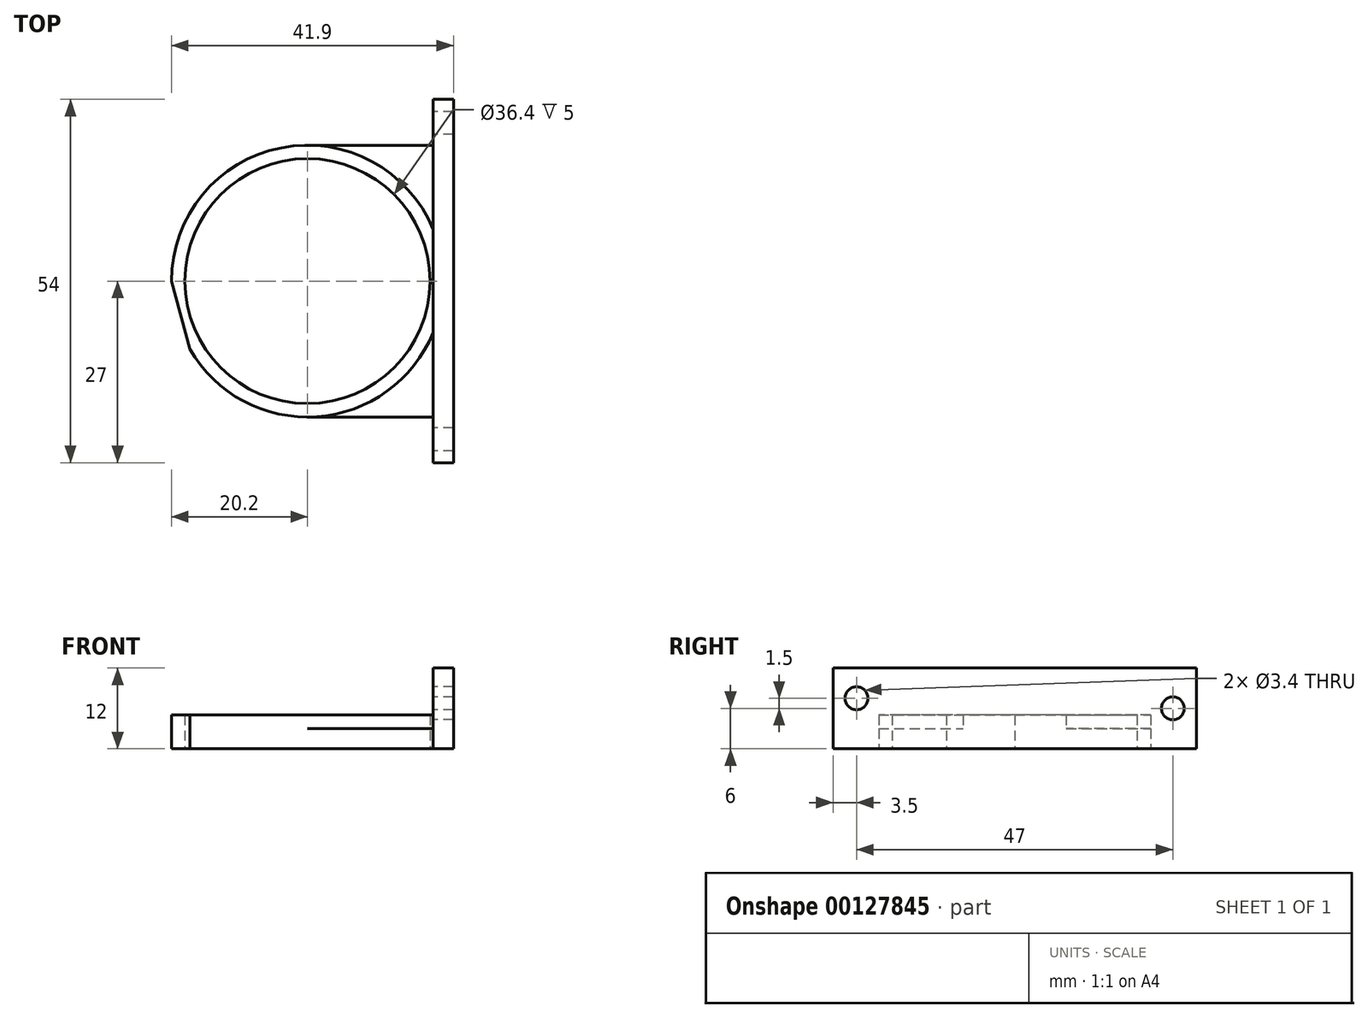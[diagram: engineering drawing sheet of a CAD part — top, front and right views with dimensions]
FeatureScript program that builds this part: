
annotation { "Feature Type Name" : "Feature", "Feature Type Description" : "" }
export const myFeature = defineFeature(function(context is Context, id is Id, definition is map)
    precondition{}
    {
        {
            var Q0;
            Q0=qCreatedBy(makeId("Top.planeOp"),FACE);
            var sketch = newSketch(context, id + "F0", { "sketchPlane" : qUnion([Q0])});
            skCircle(sketch, "E0", {"center": v(0, 0) * mm, "radius": 20.2 * mm});
            skLineSegment(sketch, "E1.bottom", {"start": v(0, 20.2) * mm, "end": v(21.7, 20.2) * mm});
            skLineSegment(sketch, "E1.top", {"start": v(0, -20.2) * mm, "end": v(21.7, -20.2) * mm});
            skLineSegment(sketch, "E1.left", {"start": v(0, 20.2) * mm, "end": v(0, -20.2) * mm});
            skLineSegment(sketch, "E1.right", {"start": v(21.7, 20.2) * mm, "end": v(21.7, -20.2) * mm});
            skLineSegment(sketch, "E2.bottom", {"start": v(21.7, 27) * mm, "end": v(18.7, 27) * mm});
            skLineSegment(sketch, "E2.top", {"start": v(21.7, 0) * mm, "end": v(18.7, 0) * mm});
            skLineSegment(sketch, "E2.left", {"start": v(21.7, 27) * mm, "end": v(21.7, 0) * mm});
            skLineSegment(sketch, "E2.right", {"start": v(18.7, 27) * mm, "end": v(18.7, 0) * mm});
            skLineSegment(sketch, "E3.MirrorCS", {"start": v(21.7, -27) * mm, "end": v(18.7, -27) * mm});
            skLineSegment(sketch, "E4.MirrorCS", {"start": v(18.7, -27) * mm, "end": v(18.7, 0) * mm});
            skLineSegment(sketch, "E5.MirrorCS", {"start": v(21.7, -27) * mm, "end": v(21.7, 0) * mm});
            skCircle(sketch, "E6", {"center": v(0, 0) * mm, "radius": 18.2 * mm});
            skCircle(sketch, "E7.cCircle", {"center": v(0, 0) * mm, "radius": 12.5 * mm, "construction": true});
            skLineSegment(sketch, "E7.0", {"start": v(-8.84, 8.84) * mm, "end": v(8.84, 8.84) * mm});
            skLineSegment(sketch, "E7.1", {"start": v(8.84, 8.84) * mm, "end": v(8.84, -8.84) * mm});
            skLineSegment(sketch, "E7.2", {"start": v(8.84, -8.84) * mm, "end": v(-8.84, -8.84) * mm});
            skLineSegment(sketch, "E7.3", {"start": v(-8.84, -8.84) * mm, "end": v(-8.84, 8.84) * mm});
            skCircle(sketch, "E8", {"center": v(-8.84, -8.84) * mm, "radius": 1.5 * mm});
            skCircle(sketch, "E9", {"center": v(8.84, -8.84) * mm, "radius": 1.5 * mm});
            skCircle(sketch, "E10", {"center": v(8.84, 8.84) * mm, "radius": 1.5 * mm});
            skCircle(sketch, "E11", {"center": v(-8.84, 8.84) * mm, "radius": 1.5 * mm});
            skPoint(sketch, "E12", {"position": v(0, -30) * mm});
            skPoint(sketch, "E13", {"position": v(21.7, -30) * mm});
            skLineSegment(sketch, "E14", {"start": v(21.7, -30) * mm, "end": v(-2.2, -30) * mm});
            skCircle(sketch, "E15", {"center": v(-2.2, -30) * mm, "radius": 6.5 * mm});
            skCircle(sketch, "E16", {"center": v(-2.2, -30) * mm, "radius": 10 * mm});
            skLineSegment(sketch, "E17", {"start": v(-20.2, 0) * mm, "end": v(-12.2, -29.82) * mm});
            skPoint(sketch, "E17.startSnap0", {"position": v(-8.84, 0) * mm});
            skLineSegment(sketch, "E18", {"start": v(7.8, -30) * mm, "end": v(18.7, -20.2) * mm});
            skCircle(sketch, "E19", {"center": v(0, 0) * mm, "radius": 5.8 * mm});
            skSolve(sketch);
        }
        {
            var Q0;
            {var subQ5=sQuery(id+"F0.wireOp",EDGE,"E2.bottom");Q0=makeQuery(id+"F0.imprint","IMPRINT",FACE,{"disambiguationData":[TD([[makeQuery(id+"F0.imprint","IMPRINT",EDGE,{"derivedFrom":subQ5}),1.0]])]});}
            var Q1;
            {var subQ5=sQuery(id+"F0.wireOp",EDGE,"E0");var subQ7=sQuery(id+"F0.wireOp",EDGE,"E2.right");var subQ9=makeQuery(id+"F0.imprint","INTERSECT",VERTEX,{"derivedFrom":[subQ5,subQ7]});Q1=makeQuery(id+"F0.imprint","IMPRINT",FACE,{"disambiguationData":[TD([[makeQuery(id+"F0.imprint","IMPRINT",EDGE,{"disambiguationData":[TD([[subQ9,1.0]])],"derivedFrom":subQ5}),-1.0]])]});}
            var Q2;
            {var subQ3=sQuery(id+"F0.wireOp",EDGE,"E0");var subQ7=sQuery(id+"F0.wireOp",EDGE,"E2.top");var subQ9=makeQuery(id+"F0.imprint","INTERSECT",VERTEX,{"derivedFrom":[subQ3,subQ7]});Q2=makeQuery(id+"F0.imprint","IMPRINT",FACE,{"disambiguationData":[TD([[makeQuery(id+"F0.imprint","IMPRINT",EDGE,{"disambiguationData":[TD([[subQ9,1.0]])],"derivedFrom":subQ3}),-1.0]])]});}
            var Q3;
            {var subQ5=sQuery(id+"F0.wireOp",EDGE,"E3.MirrorCS");Q3=makeQuery(id+"F0.imprint","IMPRINT",FACE,{"disambiguationData":[TD([[makeQuery(id+"F0.imprint","IMPRINT",EDGE,{"derivedFrom":subQ5}),-1.0]])]});}
            var Q4;
            {var subQ0=sQuery(id+"F0.wireOp",EDGE,"E2.right");var subQ1=sQuery(id+"F0.wireOp",EDGE,"E0");var subQ2=makeQuery(id+"F0.imprint","INTERSECT",VERTEX,{"derivedFrom":[subQ1,subQ0]});Q4=makeQuery(id+"F0.imprint","IMPRINT",FACE,{"disambiguationData":[TD([[makeQuery(id+"F0.imprint","IMPRINT",EDGE,{"disambiguationData":[TD([[subQ2,1.0]])],"derivedFrom":subQ1}),1.0]])]});}
            var Q5;
            {var subQ0=sQuery(id+"F0.wireOp",EDGE,"E2.top");var subQ1=sQuery(id+"F0.wireOp",EDGE,"E0");var subQ2=makeQuery(id+"F0.imprint","INTERSECT",VERTEX,{"derivedFrom":[subQ1,subQ0]});Q5=makeQuery(id+"F0.imprint","IMPRINT",FACE,{"disambiguationData":[TD([[makeQuery(id+"F0.imprint","IMPRINT",EDGE,{"disambiguationData":[TD([[subQ2,1.0]])],"derivedFrom":subQ1}),1.0]])]});}
            extrude(context, id + "F1", {"entities" : qUnion([Q0, Q1, Q2, Q3, Q4, Q5]), "depth" : 12 * mm});
        }
        {
            var Q0;
            {var subQ0=sQuery(id+"F0.wireOp",EDGE,"E1.left");var subQ3=sQuery(id+"F0.wireOp",EDGE,"E6");var subQ4=makeQuery(id+"F0.imprint","INTERSECT",VERTEX,{"disambiguationData":[OD(0.0)],"derivedFrom":[subQ0,subQ3]});Q0=makeQuery(id+"F0.imprint","IMPRINT",FACE,{"disambiguationData":[TD([[makeQuery(id+"F0.imprint","IMPRINT",EDGE,{"disambiguationData":[TD([[subQ4,-1.0]])],"derivedFrom":subQ3}),-1.0]])]});}
            var Q1;
            {var subQ0=sQuery(id+"F0.wireOp",EDGE,"E1.left");var subQ3=sQuery(id+"F0.wireOp",EDGE,"E6");var subQ4=makeQuery(id+"F0.imprint","INTERSECT",VERTEX,{"disambiguationData":[OD(0.0)],"derivedFrom":[subQ0,subQ3]});Q1=makeQuery(id+"F0.imprint","IMPRINT",FACE,{"disambiguationData":[TD([[makeQuery(id+"F0.imprint","IMPRINT",EDGE,{"disambiguationData":[TD([[subQ4,1.0]])],"derivedFrom":subQ3}),-1.0]])]});}
            var Q2;
            {var subQ0=sQuery(id+"F0.wireOp",EDGE,"E17");var subQ1=sQuery(id+"F0.wireOp",EDGE,"E0");var subQ2=makeQuery(id+"F0.imprint","INTERSECT",VERTEX,{"disambiguationData":[OD(0.0)],"derivedFrom":[subQ1,subQ0]});Q2=makeQuery(id+"F0.imprint","IMPRINT",FACE,{"disambiguationData":[TD([[makeQuery(id+"F0.imprint","IMPRINT",EDGE,{"disambiguationData":[TD([[subQ2,-1.0]])],"derivedFrom":subQ1}),1.0]])]});}
            extrude(context, id + "F2", {"entities" : qUnion([Q0, Q1, Q2]), "operationType" : NewBodyOperationType.ADD, "depth" : 5 * mm});
        }
        {
            var Q0;
            {var subQ1=sQuery(id+"F0.wireOp",EDGE,"E1.left");var subQ5=sQuery(id+"F0.wireOp",EDGE,"E6");var subQ6=makeQuery(id+"F0.imprint","INTERSECT",VERTEX,{"disambiguationData":[OD(0.0)],"derivedFrom":[subQ1,subQ5]});Q0=makeQuery(id+"F0.imprint","IMPRINT",FACE,{"disambiguationData":[TD([[makeQuery(id+"F0.imprint","IMPRINT",EDGE,{"disambiguationData":[TD([[subQ6,-1.0]])],"derivedFrom":subQ1}),-1.0]])]});}
            var Q1;
            {var subQ6=sQuery(id+"F0.wireOp",EDGE,"E1.left");var subQ9=sQuery(id+"F0.wireOp",EDGE,"E7.0");var subQ10=makeQuery(id+"F0.imprint","INTERSECT",VERTEX,{"derivedFrom":[subQ6,subQ9]});Q1=makeQuery(id+"F0.imprint","IMPRINT",FACE,{"disambiguationData":[TD([[makeQuery(id+"F0.imprint","IMPRINT",EDGE,{"disambiguationData":[TD([[subQ10,-1.0]])],"derivedFrom":subQ6}),1.0]])]});}
            var Q2;
            {var subQ0=sQuery(id+"F0.wireOp",EDGE,"E7.0");var subQ1=sQuery(id+"F0.wireOp",EDGE,"E1.left");var subQ2=makeQuery(id+"F0.imprint","INTERSECT",VERTEX,{"derivedFrom":[subQ1,subQ0]});Q2=makeQuery(id+"F0.imprint","IMPRINT",FACE,{"disambiguationData":[TD([[makeQuery(id+"F0.imprint","IMPRINT",EDGE,{"disambiguationData":[TD([[subQ2,-1.0]])],"derivedFrom":subQ1}),-1.0]])]});}
            var Q3;
            {var subQ1=sQuery(id+"F0.wireOp",EDGE,"E1.left");var subQ7=sQuery(id+"F0.wireOp",EDGE,"E6");var subQ9=makeQuery(id+"F0.imprint","INTERSECT",VERTEX,{"disambiguationData":[OD(0.0)],"derivedFrom":[subQ1,subQ7]});Q3=makeQuery(id+"F0.imprint","IMPRINT",FACE,{"disambiguationData":[TD([[makeQuery(id+"F0.imprint","IMPRINT",EDGE,{"disambiguationData":[TD([[subQ9,-1.0]])],"derivedFrom":subQ1}),1.0]])]});}
            extrude(context, id + "F3", {"entities" : qUnion([Q0, Q1, Q2, Q3]), "operationType" : NewBodyOperationType.ADD, "depth" : 3 * mm});
        }
        {
            var Q0;
            {var subQ0=sQuery(id+"F0.wireOp",EDGE,"E16");var subQ1=sQuery(id+"F0.wireOp",EDGE,"E0");var subQ2=makeQuery(id+"F0.imprint","INTERSECT",VERTEX,{"disambiguationData":[OD(0.0)],"derivedFrom":[subQ1,subQ0]});Q0=makeQuery(id+"F0.imprint","IMPRINT",FACE,{"disambiguationData":[TD([[makeQuery(id+"F0.imprint","IMPRINT",EDGE,{"disambiguationData":[TD([[subQ2,-1.0]])],"derivedFrom":subQ1}),1.0]])]});}
            var Q1;
            Q1=makeQuery(id+"F0.imprint","IMPRINT",FACE,{"disambiguationData":[TD([[makeQuery(id+"F0.imprint","IMPRINT",EDGE,{"derivedFrom":sQuery(id+"F0.wireOp",EDGE,"E15")}),-1.0]])]});
            extrude(context, id + "F4", {"entities" : qUnion([Q0, Q1]), "operationType" : NewBodyOperationType.ADD, "depth" : 5 * mm});
        }
        {
            var Q0;
            {var subQ0=sQuery(id+"F0.wireOp",EDGE,"E17");var subQ1=sQuery(id+"F0.wireOp",EDGE,"E0");var subQ2=makeQuery(id+"F0.imprint","INTERSECT",VERTEX,{"disambiguationData":[OD(1.0)],"derivedFrom":[subQ1,subQ0]});Q0=makeQuery(id+"F0.imprint","IMPRINT",FACE,{"disambiguationData":[TD([[makeQuery(id+"F0.imprint","IMPRINT",EDGE,{"disambiguationData":[TD([[subQ2,-1.0]])],"derivedFrom":subQ1}),-1.0]])]});}
            var Q1;
            {var subQ1=sQuery(id+"F0.wireOp",EDGE,"E0");var subQ3=sQuery(id+"F0.wireOp",EDGE,"E4.MirrorCS");var subQ4=makeQuery(id+"F0.imprint","INTERSECT",VERTEX,{"derivedFrom":[subQ1,subQ3]});Q1=makeQuery(id+"F0.imprint","IMPRINT",FACE,{"disambiguationData":[TD([[makeQuery(id+"F0.imprint","IMPRINT",EDGE,{"disambiguationData":[TD([[subQ4,1.0]])],"derivedFrom":subQ1}),-1.0]])]});}
            var Q2;
            {var subQ5=sQuery(id+"F0.wireOp",EDGE,"E18");Q2=makeQuery(id+"F0.imprint","IMPRINT",FACE,{"disambiguationData":[TD([[makeQuery(id+"F0.imprint","IMPRINT",EDGE,{"derivedFrom":subQ5}),1.0]])]});}
            extrude(context, id + "F5", {"entities" : qUnion([Q0, Q1, Q2]), "operationType" : NewBodyOperationType.ADD, "depth" : 3 * mm});
        }
        {
            var Q0;
            Q0=makeQuery(id+"F1.opExtrude","SWEPT_FACE",FACE,{"disambiguationData":[OSD([sQuery(id+"F0.wireOp",EDGE,"E2.right"),sQuery(id+"F0.wireOp",EDGE,"E4.MirrorCS")])]});
            var sketch = newSketch(context, id + "F6", { "sketchPlane" : qUnion([Q0])});
            skPoint(sketch, "E20", {"position": v(-23.5, 6) * mm});
            skLineSegment(sketch, "E21", {"start": v(-23.5, 6) * mm, "end": v(-27, 6) * mm});
            skLineSegment(sketch, "E22", {"start": v(-23.5, 6) * mm, "end": v(-23.5, 12) * mm});
            skCircle(sketch, "E23", {"center": v(-23.5, 6) * mm, "radius": 1.7 * mm});
            skLineSegment(sketch, "E24", {"start": v(-27, 6) * mm, "end": v(0, 6) * mm});
            skPoint(sketch, "E24.endSnap0", {"position": v(0, 5) * mm});
            skLineSegment(sketch, "E25", {"start": v(0, 6) * mm, "end": v(0, 12) * mm});
            skCircle(sketch, "E26.MirrorC", {"center": v(23.5, 7.5) * mm, "radius": 1.7 * mm});
            skLineSegment(sketch, "E27", {"start": v(23.5, 7.5) * mm, "end": v(23.5, 12) * mm});
            skSolve(sketch);
        }
        {
            var Q0;
            {var subQ0=sQuery(id+"F6.wireOp",EDGE,"E24");var subQ1=sQuery(id+"F6.wireOp",EDGE,"E22");var subQ2=makeQuery(id+"F6.imprint","INTERSECT",VERTEX,{"derivedFrom":[subQ1,subQ0]});Q0=makeQuery(id+"F6.imprint","IMPRINT",FACE,{"disambiguationData":[TD([[makeQuery(id+"F6.imprint","IMPRINT",EDGE,{"disambiguationData":[TD([[subQ2,-1.0]])],"derivedFrom":subQ1}),1.0]])]});}
            var Q1;
            {var subQ0=sQuery(id+"F6.wireOp",EDGE,"E24");var subQ1=sQuery(id+"F6.wireOp",EDGE,"E23");var subQ2=makeQuery(id+"F6.imprint","INTERSECT",VERTEX,{"disambiguationData":[OD(0.0)],"derivedFrom":[subQ1,subQ0]});Q1=makeQuery(id+"F6.imprint","IMPRINT",FACE,{"disambiguationData":[TD([[makeQuery(id+"F6.imprint","IMPRINT",EDGE,{"disambiguationData":[TD([[subQ2,1.0]])],"derivedFrom":subQ1}),1.0]])]});}
            var Q2;
            {var subQ0=sQuery(id+"F6.wireOp",EDGE,"E24");var subQ1=sQuery(id+"F6.wireOp",EDGE,"E22");var subQ2=makeQuery(id+"F6.imprint","INTERSECT",VERTEX,{"derivedFrom":[subQ1,subQ0]});Q2=makeQuery(id+"F6.imprint","IMPRINT",FACE,{"disambiguationData":[TD([[makeQuery(id+"F6.imprint","IMPRINT",EDGE,{"disambiguationData":[TD([[subQ2,-1.0]])],"derivedFrom":subQ1}),-1.0]])]});}
            extrude(context, id + "F7", {"entities" : qUnion([Q0, Q1, Q2]), "operationType" : NewBodyOperationType.REMOVE, "oppositeDirection" : true, "depth" : 25 * mm});
        }
        {
            var Q0;
            Q0=qSketchRegion(id+"F6",true);
            extrude(context, id + "F8", {"entities" : qUnion([Q0]), "operationType" : NewBodyOperationType.REMOVE, "oppositeDirection" : true, "depth" : 25 * mm});
        }
        {
            var Q0;
            {var subQ0=sQuery(id+"F0.wireOp",EDGE,"E1.bottom");var subQ3=sQuery(id+"F0.wireOp",EDGE,"E2.right");var subQ5=makeQuery(id+"F0.imprint","INTERSECT",VERTEX,{"derivedFrom":[subQ0,subQ3]});Q0=makeQuery(id+"F0.imprint","IMPRINT",FACE,{"disambiguationData":[TD([[makeQuery(id+"F0.imprint","IMPRINT",EDGE,{"disambiguationData":[TD([[subQ5,-1.0]])],"derivedFrom":subQ3}),-1.0]])]});}
            extrude(context, id + "F9", {"entities" : qUnion([Q0]), "operationType" : NewBodyOperationType.ADD, "depth" : 3 * mm});
        }
        {
            var Q0;
            Q0=makeQuery(id+"F1.opExtrude","SWEPT_BODY",BODY,{"disambiguationData":[OSD([sQuery(id+"F0.wireOp",EDGE,"E2.bottom"),sQuery(id+"F0.wireOp",EDGE,"E2.left"),sQuery(id+"F0.wireOp",EDGE,"E2.right"),sQuery(id+"F0.wireOp",EDGE,"E3.MirrorCS"),sQuery(id+"F0.wireOp",EDGE,"E4.MirrorCS"),sQuery(id+"F0.wireOp",EDGE,"E5.MirrorCS")])]});
            transform(context, id + "F10", {"entities" : qUnion([Q0]), "transformType" : TransformType.TRANSLATION_3D, "dx" : 0 * mm, "dy" : 0 * mm, "dz" : 0 * mm, "makeCopy" : true});
        }
        {
            var Q0;
            Q0=makeQuery(id+"F1.opExtrude","SWEPT_BODY",BODY,{"disambiguationData":[OSD([sQuery(id+"F0.wireOp",EDGE,"E2.bottom"),sQuery(id+"F0.wireOp",EDGE,"E2.left"),sQuery(id+"F0.wireOp",EDGE,"E2.right"),sQuery(id+"F0.wireOp",EDGE,"E3.MirrorCS"),sQuery(id+"F0.wireOp",EDGE,"E4.MirrorCS"),sQuery(id+"F0.wireOp",EDGE,"E5.MirrorCS")])]});
            deleteBodies(context, id + "F11", {"entities" : qUnion([Q0])});
        }
        {
            var Q0;
            Q0=makeQuery(id+"F10.opPattern","COPY",FACE,{"derivedFrom":makeQuery(id+"F3.opExtrude","CAP_FACE",FACE,{"disambiguationData":[OSD([sQuery(id+"F0.wireOp",EDGE,"E6"),sQuery(id+"F0.wireOp",EDGE,"E8"),sQuery(id+"F0.wireOp",EDGE,"E9"),sQuery(id+"F0.wireOp",EDGE,"E10"),sQuery(id+"F0.wireOp",EDGE,"E11"),sQuery(id+"F0.wireOp",EDGE,"E19")])],"isStart":false}),"instanceName":"1"});
            extrude(context, id + "F12", {"entities" : qUnion([Q0]), "operationType" : NewBodyOperationType.REMOVE, "oppositeDirection" : true, "depth" : 25 * mm});
        }
        {
            var Q0;
            Q0=makeQuery(id+"F0.imprint","IMPRINT",FACE,{"disambiguationData":[TD([[makeQuery(id+"F0.imprint","IMPRINT",EDGE,{"derivedFrom":sQuery(id+"F0.wireOp",EDGE,"E15")}),-1.0]])]});
            var Q1;
            {var subQ5=sQuery(id+"F0.wireOp",EDGE,"E18");Q1=makeQuery(id+"F0.imprint","IMPRINT",FACE,{"disambiguationData":[TD([[makeQuery(id+"F0.imprint","IMPRINT",EDGE,{"derivedFrom":subQ5}),1.0]])]});}
            var Q2;
            {var subQ0=sQuery(id+"F0.wireOp",EDGE,"E17");var subQ1=sQuery(id+"F0.wireOp",EDGE,"E0");var subQ2=makeQuery(id+"F0.imprint","INTERSECT",VERTEX,{"disambiguationData":[OD(1.0)],"derivedFrom":[subQ1,subQ0]});Q2=makeQuery(id+"F0.imprint","IMPRINT",FACE,{"disambiguationData":[TD([[makeQuery(id+"F0.imprint","IMPRINT",EDGE,{"disambiguationData":[TD([[subQ2,-1.0]])],"derivedFrom":subQ1}),-1.0]])]});}
            var Q3;
            {var subQ0=sQuery(id+"F0.wireOp",EDGE,"E1.bottom");var subQ3=sQuery(id+"F0.wireOp",EDGE,"E2.right");var subQ5=makeQuery(id+"F0.imprint","INTERSECT",VERTEX,{"derivedFrom":[subQ0,subQ3]});Q3=makeQuery(id+"F0.imprint","IMPRINT",FACE,{"disambiguationData":[TD([[makeQuery(id+"F0.imprint","IMPRINT",EDGE,{"disambiguationData":[TD([[subQ5,-1.0]])],"derivedFrom":subQ3}),-1.0]])]});}
            extrude(context, id + "F13", {"entities" : qUnion([Q0, Q1, Q2, Q3]), "operationType" : NewBodyOperationType.REMOVE, "depth" : 25 * mm});
        }
        {
            var Q0;
            {var subQ0=sQuery(id+"F0.wireOp",EDGE,"E1.bottom");var subQ3=sQuery(id+"F0.wireOp",EDGE,"E2.right");var subQ5=makeQuery(id+"F0.imprint","INTERSECT",VERTEX,{"derivedFrom":[subQ0,subQ3]});Q0=makeQuery(id+"F0.imprint","IMPRINT",FACE,{"disambiguationData":[TD([[makeQuery(id+"F0.imprint","IMPRINT",EDGE,{"disambiguationData":[TD([[subQ5,-1.0]])],"derivedFrom":subQ3}),-1.0]])]});}
            extrude(context, id + "F14", {"entities" : qUnion([Q0]), "operationType" : NewBodyOperationType.ADD, "depth" : 3 * mm});
        }
    });
